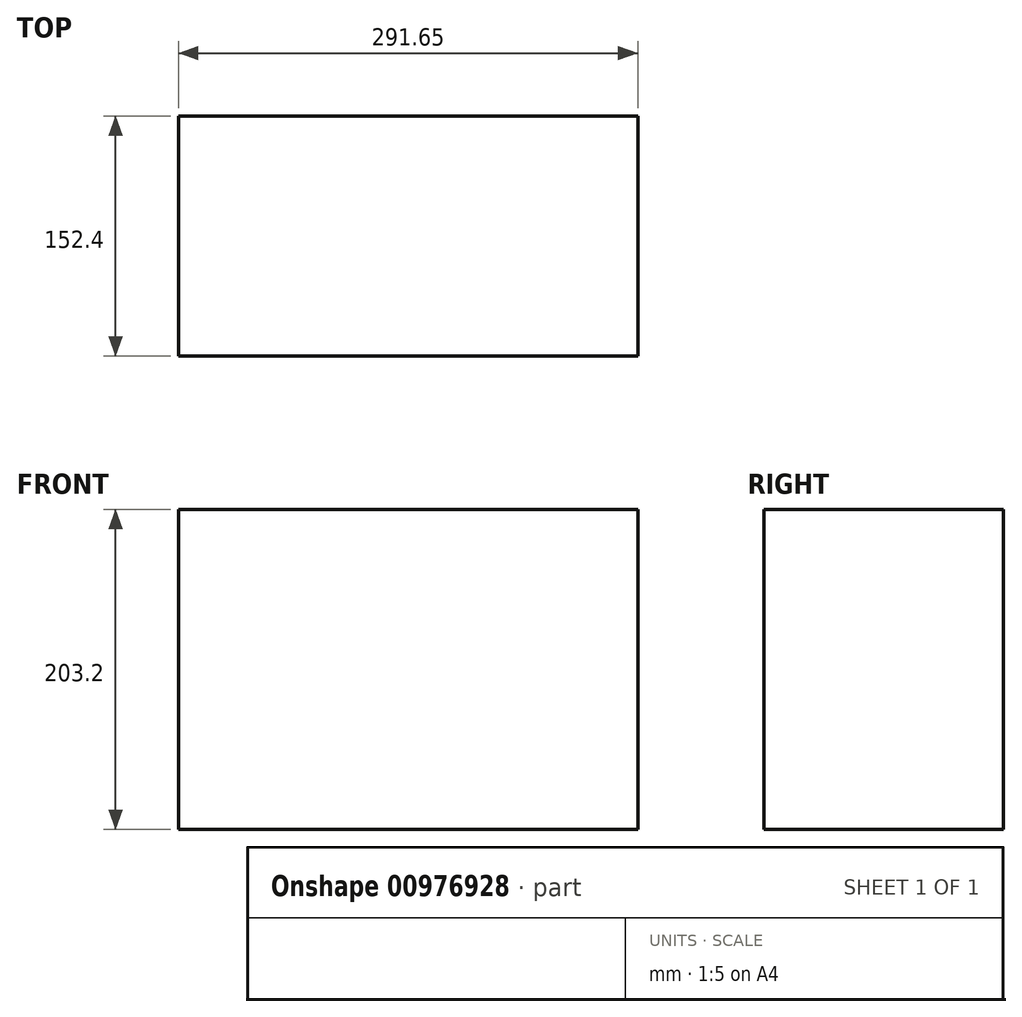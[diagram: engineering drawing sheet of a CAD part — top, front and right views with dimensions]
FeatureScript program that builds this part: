
annotation { "Feature Type Name" : "Feature", "Feature Type Description" : "" }
export const myFeature = defineFeature(function(context is Context, id is Id, definition is map)
    precondition{}
    {
        {
            var Q0;
            Q0=qCreatedBy(makeId("Front.planeOp"),FACE);
            var sketch = newSketch(context, id + "F0", { "sketchPlane" : qUnion([Q0])});
            skLineSegment(sketch, "E0.bottom", {"start": v(70.54, -53.4) * mm, "end": v(-221.11, -53.4) * mm});
            skLineSegment(sketch, "E0.top", {"start": v(70.54, 149.8) * mm, "end": v(-221.11, 149.8) * mm});
            skLineSegment(sketch, "E0.left", {"start": v(70.54, -53.4) * mm, "end": v(70.54, 149.8) * mm});
            skLineSegment(sketch, "E0.right", {"start": v(-221.11, -53.4) * mm, "end": v(-221.11, 149.8) * mm});
            skPoint(sketch, "E0.middle", {"position": v(-75.29, 48.2) * mm});
            skSolve(sketch);
        }
        {
            var Q0;
            Q0 = qSketchRegion(id + "F0", true);
            extrude(context, id + "F1", {"entities" : qUnion([Q0]), "depth" : 152.4 * mm, "offsetDistance" : 25.4 * mm});
        }
    });
